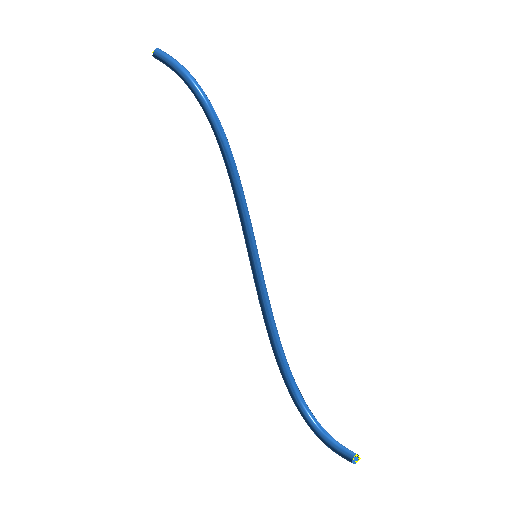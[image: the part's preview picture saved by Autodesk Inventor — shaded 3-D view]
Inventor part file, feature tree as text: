
AUTODESK INVENTOR PART (.ipt)
format: ipt  version: 2022 (Build 260153000, 153)  size: 135,168 bytes
history: native  units: mm (DEFAULTED — no unit token found)
features: other x6, plane x1, sketch x1, sweep x1
ambient origin geometry x8: Origin, YZ Plane, XZ Plane, XY Plane, X Axis, Y Axis, Z Axis, Center Point
bodies: Body1 (feature_tree)
feature tree (9):
  other  "Work Point1"
  other  "Work Point2"
  other  "Wire1"
  other  "Work Point3"
  other  "Work Point4"
  plane  "Work Plane1"
  sketch  "Sketch1"  dims[d0=0.0mm d1=0.0mm]
  other  "Srf1"
  sweep  "SweepSrf1"
